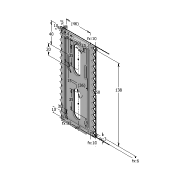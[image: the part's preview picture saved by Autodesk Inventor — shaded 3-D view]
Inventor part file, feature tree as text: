
AUTODESK INVENTOR PART (.ipt)
format: ipt  version: 2022 (Build 260153000, 153)  size: 234,496 bytes
history: native  units: mm
features: extrude x3, sketch x1, fillet x1
ambient origin geometry x8: Origin, YZ Plane, XZ Plane, XY Plane, X Axis, Y Axis, Z Axis, Center Point
bodies: Solid1 (feature_tree)
feature tree (5):
  sketch  "Sketch1"  dims[d0=66.0mm d1=150.0mm d2=45.0deg d3=5.0mm d4=150.0mm d6=10.0mm d7=10.0mm d9=10.0mm d11=33.0mm d12=10.0mm d13=10.0mm d14=3.0mm d15=10.0mm d16=3.0mm d17=138.0mm d19=6.0mm d20=3.2mm d21=11.0mm d22=10.0mm d23=10.0mm d24=46.0mm d25=3.0mm d26=4.0mm d27=40.0mm d28=20.0mm d29=30.0mm d30=36.0mm d31=2.5mm d32=0.0mm d33=8.0mm d34=0.0mm d35=3.0mm d36=35.0mm d37=15.0mm d38=15.0mm d39=35.0mm d40=15.0mm d41=15.0mm d42=0.0mm d43=0.0mm]
  extrude  "Extrusion1"  Depth=150.0mm
  extrude  "Extrusion2"  TaperAngle=45.0deg  [1 undecoded]
  fillet  "Fillet1"  Radius=5.0mm
  extrude  "Extrusion3"  Depth=150.0mm
note: 1 required parameter value undecoded (feature->parameter linkage not recoverable at this tier; creation-order binding heuristic only, values carry confidence <= 0.55)
